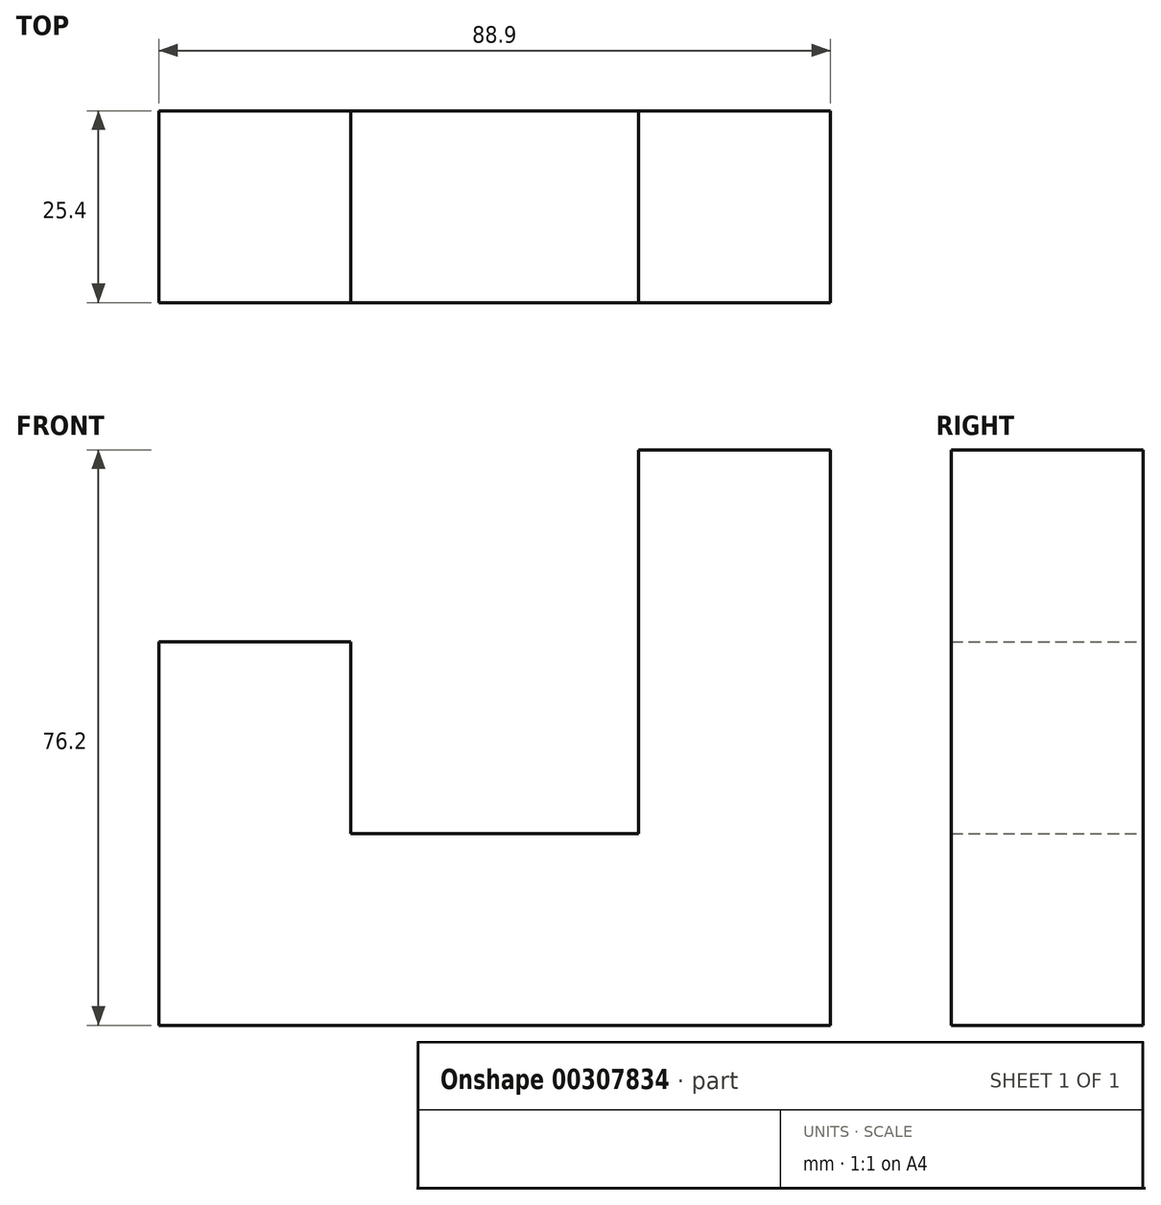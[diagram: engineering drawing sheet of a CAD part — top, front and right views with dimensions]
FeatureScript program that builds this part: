
annotation { "Feature Type Name" : "Feature", "Feature Type Description" : "" }
export const myFeature = defineFeature(function(context is Context, id is Id, definition is map)
    precondition{}
    {
        {
            var Q0;
            Q0=qCreatedBy(makeId("Front.planeOp"),FACE);
            var sketch = newSketch(context, id + "F0", { "sketchPlane" : qUnion([Q0])});
            skLineSegment(sketch, "E0", {"start": v(-85.71, 13.56) * mm, "end": v(-60.31, 13.56) * mm});
            skLineSegment(sketch, "E1", {"start": v(-60.31, 13.56) * mm, "end": v(-60.31, -11.84) * mm});
            skLineSegment(sketch, "E2", {"start": v(-60.31, -11.84) * mm, "end": v(-22.21, -11.84) * mm});
            skLineSegment(sketch, "E3", {"start": v(-22.21, -11.84) * mm, "end": v(-22.21, 38.96) * mm});
            skLineSegment(sketch, "E4", {"start": v(-22.21, 38.96) * mm, "end": v(3.19, 38.96) * mm});
            skLineSegment(sketch, "E5", {"start": v(3.19, 38.96) * mm, "end": v(3.19, -37.24) * mm});
            skLineSegment(sketch, "E6", {"start": v(3.19, -37.24) * mm, "end": v(-85.71, -37.24) * mm});
            skLineSegment(sketch, "E7", {"start": v(-85.71, 13.56) * mm, "end": v(-85.71, -37.24) * mm});
            skSolve(sketch);
        }
        {
            var Q0;
            Q0=makeQuery(id+"F0.imprint","IMPRINT",FACE,{"disambiguationData":[TD([[makeQuery(id+"F0.imprint","IMPRINT",EDGE,{"derivedFrom":sQuery(id+"F0.wireOp",EDGE,"E0")}),-1.0]])]});
            extrude(context, id + "F1", {"entities" : qUnion([Q0]), "depth" : 25.4 * mm});
        }
    });
